# Revit family: EKF_EE_ОпорныеУглыЦоколяTrivia_AVERES
name_source: partatom
category: Электрооборудование
units: mm (PartAtom-declared; Revit-internal decimal feet)

## family parameters
Всегда вертикально = Нет
На основе рабочей плоскости = Да
Общий = Да
При загрузке вырезать с полостями = Нет
Размер круглого соединителя = Использовать диаметр
Тип детали = Силовой щит
Точка расчета площади = Нет

## types (2) — shared parameters
ADSK_Единица измерения = шт.
ADSK_Завод-изготовитель = EKF
ADSK_Количество = 1
ADSK_Марка = 4 опорных угла цоколя
ADSK_Материал = RAL 7035_Сталь
ADSK_Обозначение = 4 опорных угла цоколя
ADSK_Размер_Глубина = 82 мм
ADSK_Размер_Ширина = 82 мм
Изготовитель = EKF
Отметка по умолчанию = 1219.2 мм
Серия номенклатуры = Averes
Степень защиты IP = -
ТВ = EKF_2_TRIVIA_AVERES
Тип установки = -
Тип_Опоры = Вл_4 опорных угла цоколя В100 EKF AVERES
zero-valued in all types: ADSK_Масса

## per-type parameters (varying)
| type | ADSK_Код изделия | ADSK_Наименование | ADSK_Размер_Высота | Тип | Тип_Опор |
| 4 опорных угла цоколя В100 EKF AVERES | B4FW2 | 4 опорных угла цоколя В100 EKF AVERES | 100 мм | 481 мм | Вл_4 опорных угла цоколя В100 EKF AVERES |
| 4 опорных угла цоколя В200  EKF AVERES | BS200 | 4 опорных угла цоколя В200 EKF AVERES | 200 мм | 482 мм | Вл_4 опорных угла цоколя В200  EKF AVERES |
